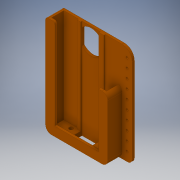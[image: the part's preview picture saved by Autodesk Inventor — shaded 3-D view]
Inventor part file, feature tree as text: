
AUTODESK INVENTOR PART (.ipt)
format: ipt  version: 2019 (Build 230136000, 136)  size: 353,280 bytes
history: native  units: in
note: dims shown in document units (in); Inventor stores cm internally (conversion verified against a paired STEP export)
features: sketch x17, extrude x15, fillet x8, projected_geometry x5, hole x1, pattern_linear x1
ambient origin geometry x8: Origin, YZ Plane, XZ Plane, XY Plane, X Axis, Y Axis, Z Axis, Center Point
bodies: Solid1 (feature_tree), body (feature_tree)
feature tree (47):
  extrude  "Extrusion2"  Depth=5.5in
  extrude  "Extrusion3"  Depth=0.5in
  extrude  "Extrusion4"  Depth=0.5in
  extrude  "Extrusion5"  Depth=0.2in
  extrude  "Extrusion6"  Depth=0.125in
  extrude  "Extrusion7"  Depth=3.0375in
  fillet  "Fillet1"  Radius=0.125in
  fillet  "Fillet2"  Radius=2.0in
  fillet  "Fillet3"  Radius=0.65in
  hole  "Hole1"  [1 undecoded]
  pattern_linear  "Rectangular Pattern1"  Count1=10 Spacing1=0.5in
  extrude  "Extrusion8"  Depth=0.25in
  sketch  "Sketch14"  dims[d27=3.5in d28=0.0in]
  fillet  "Fillet4"  Radius=4.0in
  fillet  "Fillet5"  Radius=0.25in
  fillet  "Fillet6"  Radius=0.5in
  extrude  "Extrusion13"  Depth=0.125in
  extrude  "Extrusion14"  Depth=1.6171in
  extrude  "Extrusion15"  Depth=1.615in
  extrude  "Extrusion17"  Depth=0.805in
  extrude  "Extrusion18"  Depth=0.805in
  extrude  "Extrusion19"  Depth=1.0in TaperAngle=0.0deg
  extrude  "Extrusion20"  Depth=1.0in TaperAngle=0.0deg
  extrude  "Extrusion21"  Depth=0.5065in
  fillet  "Fillet7"  Radius=1.0in
  fillet  "Fillet8"  Radius=1.35in
  sketch  "Sketch1"  dims[d0=3.4375in d1=5.5in]
  sketch  "Sketch2"  dims[d2=0.93in d3=0.0in d4=0.5in]
  sketch  "Sketch4"  dims[d5=0.5in d6=0.5in]
  sketch  "Sketch6"  dims[d7=0.65in d8=0.0in d9=0.2in]
  projected_geometry  "Projected Loop2"
  sketch  "Sketch7"  dims[d10=0.2in d12=0.125in]
  projected_geometry  "Projected Loop3"
  sketch  "Sketch8"  dims[d13=5.25in d14=0.0in d15=3.0375in d17=0.125in d18=2.0in d19=0.65in d20=0.0in]
  sketch  "Sketch9"  dims[d21=0.55in d22=0.0in d23=0.8in]
  sketch  "Sketch13"  dims[d24=5.5in d25=0.0in]
  sketch  "Sketch18"  dims[d29=0.5625in]
  sketch  "Sketch19"  dims[d30=0.3125in]
  projected_geometry  "Projected Loop5"
  sketch  "Sketch20"  dims[d31=0.3125in]
  sketch  "Sketch21"  dims[d32=0.275in d33=1.0in]
  projected_geometry  "Projected Loop6"
  projected_geometry  "Projected Loop7"
  sketch  "Sketch22"  dims[d34=0.13in d35=0.75in d36=0.375in d37=0.25in d38=0.5635in d39=1.0in d40=0.8108in d41=3.937in d43=0.5in]
  sketch  "Sketch24"  dims[d44=0.9in d45=0.9in d46=4.0in d47=0.0in d56=0.25in d57=0.5in]
  sketch  "Sketch26"  dims[d58=0.125in d59=0.125in]
  sketch  "Sketch28"  dims[d60=0.08in d61=0.0in d63=1.6171in d64=1.615in d65=0.805in d66=0.805in d67=1.0in d68=0.0in d69=1.0in d70=0.0in d73=0.5065in d74=1.0in d75=0.0in d76=1.35in d77=0.5065in d78=1.0in d79=0.0in d80=1.0in d81=0.0in d82=1.0in d83=0.0in d84=0.75in d85=1.0in d86=0.0in d87=0.125in d88=0.3125in]
note: 1 required parameter value undecoded (feature->parameter linkage not recoverable at this tier; creation-order binding heuristic only, values carry confidence <= 0.55)
